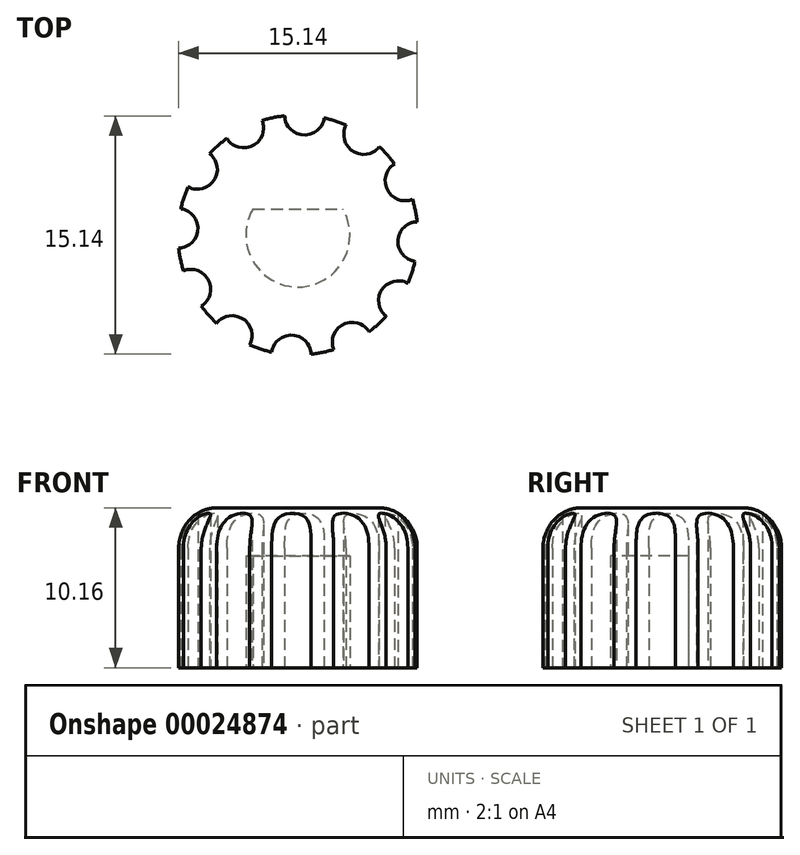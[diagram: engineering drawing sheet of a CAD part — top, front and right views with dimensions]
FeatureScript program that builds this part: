
annotation { "Feature Type Name" : "Feature", "Feature Type Description" : "" }
export const myFeature = defineFeature(function(context is Context, id is Id, definition is map)
    precondition{}
    {
        {
            var Q0;
            Q0=qCreatedBy(makeId("Top.planeOp"),FACE);
            var sketch = newSketch(context, id + "F0", { "sketchPlane" : qUnion([Q0])});
            skCircle(sketch, "E0", {"center": v(0, 0) * mm, "radius": 7.62 * mm});
            skSolve(sketch);
        }
        {
            var Q0;
            Q0=makeQuery(id+"F0.imprint","IMPRINT",FACE,{"disambiguationData":[TD([[makeQuery(id+"F0.imprint","IMPRINT",EDGE,{"derivedFrom":sQuery(id+"F0.wireOp",EDGE,"E0")}),1.0]])]});
            extrude(context, id + "F1", {"entities" : qUnion([Q0]), "oppositeDirection" : true, "depth" : 10.16 * mm});
        }
        {
            var Q0;
            Q0=makeQuery(id+"F1.opExtrude","CAP_FACE",FACE,{"disambiguationData":[OSD([sQuery(id+"F0.wireOp",EDGE,"E0")])],"isStart":false});
            var sketch = newSketch(context, id + "F2", { "sketchPlane" : qUnion([Q0])});
            skArc(sketch, "E1", {"start": v(2.86, -1.65) * mm, "mid": v(0, 3.3) * mm, "end": v(-2.86, -1.65) * mm});
            skLineSegment(sketch, "E2", {"start": v(-4.01, 3.3) * mm, "end": v(4.27, 3.3) * mm, "construction": true});
            skLineSegment(sketch, "E3", {"start": v(-2.86, -1.65) * mm, "end": v(2.86, -1.65) * mm});
            skSolve(sketch);
        }
        {
            var Q0;
            Q0=makeQuery(id+"F2.imprint","IMPRINT",FACE,{"disambiguationData":[TD([[makeQuery(id+"F2.imprint","IMPRINT",EDGE,{"derivedFrom":sQuery(id+"F2.wireOp",EDGE,"E1")}),1.0]])]});
            extrude(context, id + "F3", {"entities" : qUnion([Q0]), "operationType" : NewBodyOperationType.REMOVE, "oppositeDirection" : true, "depth" : 7.11 * mm});
        }
        {
            var Q0;
            Q0=makeQuery(id+"F1.opExtrude","CAP_EDGE",EDGE,{"disambiguationData":[OSD([sQuery(id+"F0.wireOp",EDGE,"E0")])],"isStart":true});
            fillet(context, id + "F4", {"entities" : qUnion([Q0]), "radius" : 2.54 * mm, "tangentPropagation" : true, "allowEdgeOverflow" : false});
        }
        {
            var Q0;
            Q0=makeQuery(id+"F1.opExtrude","CAP_FACE",FACE,{"disambiguationData":[OSD([sQuery(id+"F0.wireOp",EDGE,"E0")])],"isStart":false});
            var sketch = newSketch(context, id + "F5", { "sketchPlane" : qUnion([Q0])});
            skCircle(sketch, "E4", {"center": v(3.44, 6.8) * mm, "radius": 1.26 * mm});
            skCircle(sketch, "E5.1.0", {"center": v(-0.42, 7.6) * mm, "radius": 1.26 * mm});
            skCircle(sketch, "E5.2.0", {"center": v(-4.17, 6.38) * mm, "radius": 1.26 * mm});
            skCircle(sketch, "E5.3.0", {"center": v(-6.8, 3.44) * mm, "radius": 1.26 * mm});
            skCircle(sketch, "E5.4.0", {"center": v(-7.6, -0.42) * mm, "radius": 1.26 * mm});
            skCircle(sketch, "E5.5.0", {"center": v(-6.38, -4.17) * mm, "radius": 1.26 * mm});
            skCircle(sketch, "E5.6.0", {"center": v(-3.44, -6.8) * mm, "radius": 1.26 * mm});
            skCircle(sketch, "E5.7.0", {"center": v(0.42, -7.6) * mm, "radius": 1.26 * mm});
            skCircle(sketch, "E5.8.0", {"center": v(4.17, -6.38) * mm, "radius": 1.26 * mm});
            skCircle(sketch, "E5.9.0", {"center": v(6.8, -3.44) * mm, "radius": 1.26 * mm});
            skPoint(sketch, "E5.center", {"position": v(0, 0) * mm});
            skCircle(sketch, "E6.1.10.0", {"center": v(7.6, 0.42) * mm, "radius": 1.26 * mm});
            skCircle(sketch, "E7.1.11.0", {"center": v(6.38, 4.17) * mm, "radius": 1.26 * mm});
            skSolve(sketch);
        }
        {
            var Q0;
            {var subQ0=makeQuery(id+"F1.opExtrude","CAP_EDGE",EDGE,{"disambiguationData":[OSD([sQuery(id+"F0.wireOp",EDGE,"E0")])],"isStart":false});var subQ1=sQuery(id+"F5.wireOp",EDGE,"E5.2.0");var subQ3=makeQuery(id+"F5.imprint","INTERSECT",VERTEX,{"disambiguationData":[OD(0.0)],"derivedFrom":[subQ0,subQ1]});Q0=makeQuery(id+"F5.imprint","IMPRINT",FACE,{"disambiguationData":[TD([[makeQuery(id+"F5.imprint","IMPRINT",EDGE,{"disambiguationData":[TD([[subQ3,-1.0]])],"derivedFrom":subQ1}),1.0]])]});}
            var Q1;
            {var subQ0=makeQuery(id+"F1.opExtrude","CAP_EDGE",EDGE,{"disambiguationData":[OSD([sQuery(id+"F0.wireOp",EDGE,"E0")])],"isStart":false});var subQ1=sQuery(id+"F5.wireOp",EDGE,"E5.1.0");var subQ3=makeQuery(id+"F5.imprint","INTERSECT",VERTEX,{"disambiguationData":[OD(0.0)],"derivedFrom":[subQ0,subQ1]});Q1=makeQuery(id+"F5.imprint","IMPRINT",FACE,{"disambiguationData":[TD([[makeQuery(id+"F5.imprint","IMPRINT",EDGE,{"disambiguationData":[TD([[subQ3,-1.0]])],"derivedFrom":subQ1}),1.0]])]});}
            var Q2;
            {var subQ0=makeQuery(id+"F1.opExtrude","CAP_EDGE",EDGE,{"disambiguationData":[OSD([sQuery(id+"F0.wireOp",EDGE,"E0")])],"isStart":false});var subQ1=sQuery(id+"F5.wireOp",EDGE,"E4");var subQ3=makeQuery(id+"F5.imprint","INTERSECT",VERTEX,{"disambiguationData":[OD(0.0)],"derivedFrom":[subQ0,subQ1]});Q2=makeQuery(id+"F5.imprint","IMPRINT",FACE,{"disambiguationData":[TD([[makeQuery(id+"F5.imprint","IMPRINT",EDGE,{"disambiguationData":[TD([[subQ3,-1.0]])],"derivedFrom":subQ1}),1.0]])]});}
            var Q3;
            {var subQ0=makeQuery(id+"F1.opExtrude","CAP_EDGE",EDGE,{"disambiguationData":[OSD([sQuery(id+"F0.wireOp",EDGE,"E0")])],"isStart":false});var subQ1=sQuery(id+"F5.wireOp",EDGE,"E7.1.11.0");var subQ3=makeQuery(id+"F5.imprint","INTERSECT",VERTEX,{"disambiguationData":[OD(0.0)],"derivedFrom":[subQ0,subQ1]});Q3=makeQuery(id+"F5.imprint","IMPRINT",FACE,{"disambiguationData":[TD([[makeQuery(id+"F5.imprint","IMPRINT",EDGE,{"disambiguationData":[TD([[subQ3,-1.0]])],"derivedFrom":subQ1}),1.0]])]});}
            var Q4;
            {var subQ0=makeQuery(id+"F1.opExtrude","CAP_EDGE",EDGE,{"disambiguationData":[OSD([sQuery(id+"F0.wireOp",EDGE,"E0")])],"isStart":false});var subQ1=sQuery(id+"F5.wireOp",EDGE,"E6.1.10.0");var subQ3=makeQuery(id+"F5.imprint","INTERSECT",VERTEX,{"disambiguationData":[OD(0.0)],"derivedFrom":[subQ0,subQ1]});Q4=makeQuery(id+"F5.imprint","IMPRINT",FACE,{"disambiguationData":[TD([[makeQuery(id+"F5.imprint","IMPRINT",EDGE,{"disambiguationData":[TD([[subQ3,-1.0]])],"derivedFrom":subQ1}),1.0]])]});}
            var Q5;
            {var subQ0=makeQuery(id+"F1.opExtrude","CAP_EDGE",EDGE,{"disambiguationData":[OSD([sQuery(id+"F0.wireOp",EDGE,"E0")])],"isStart":false});var subQ1=sQuery(id+"F5.wireOp",EDGE,"E5.9.0");var subQ3=makeQuery(id+"F5.imprint","INTERSECT",VERTEX,{"disambiguationData":[OD(0.0)],"derivedFrom":[subQ0,subQ1]});Q5=makeQuery(id+"F5.imprint","IMPRINT",FACE,{"disambiguationData":[TD([[makeQuery(id+"F5.imprint","IMPRINT",EDGE,{"disambiguationData":[TD([[subQ3,1.0]])],"derivedFrom":subQ1}),1.0]])]});}
            var Q6;
            {var subQ0=makeQuery(id+"F1.opExtrude","CAP_EDGE",EDGE,{"disambiguationData":[OSD([sQuery(id+"F0.wireOp",EDGE,"E0")])],"isStart":false});var subQ1=sQuery(id+"F5.wireOp",EDGE,"E5.8.0");var subQ3=makeQuery(id+"F5.imprint","INTERSECT",VERTEX,{"disambiguationData":[OD(0.0)],"derivedFrom":[subQ0,subQ1]});Q6=makeQuery(id+"F5.imprint","IMPRINT",FACE,{"disambiguationData":[TD([[makeQuery(id+"F5.imprint","IMPRINT",EDGE,{"disambiguationData":[TD([[subQ3,1.0]])],"derivedFrom":subQ1}),1.0]])]});}
            var Q7;
            {var subQ0=makeQuery(id+"F1.opExtrude","CAP_EDGE",EDGE,{"disambiguationData":[OSD([sQuery(id+"F0.wireOp",EDGE,"E0")])],"isStart":false});var subQ1=sQuery(id+"F5.wireOp",EDGE,"E5.7.0");var subQ3=makeQuery(id+"F5.imprint","INTERSECT",VERTEX,{"disambiguationData":[OD(0.0)],"derivedFrom":[subQ0,subQ1]});Q7=makeQuery(id+"F5.imprint","IMPRINT",FACE,{"disambiguationData":[TD([[makeQuery(id+"F5.imprint","IMPRINT",EDGE,{"disambiguationData":[TD([[subQ3,1.0]])],"derivedFrom":subQ1}),1.0]])]});}
            var Q8;
            {var subQ0=makeQuery(id+"F1.opExtrude","CAP_EDGE",EDGE,{"disambiguationData":[OSD([sQuery(id+"F0.wireOp",EDGE,"E0")])],"isStart":false});var subQ1=sQuery(id+"F5.wireOp",EDGE,"E5.6.0");var subQ3=makeQuery(id+"F5.imprint","INTERSECT",VERTEX,{"disambiguationData":[OD(0.0)],"derivedFrom":[subQ0,subQ1]});Q8=makeQuery(id+"F5.imprint","IMPRINT",FACE,{"disambiguationData":[TD([[makeQuery(id+"F5.imprint","IMPRINT",EDGE,{"disambiguationData":[TD([[subQ3,1.0]])],"derivedFrom":subQ1}),1.0]])]});}
            var Q9;
            {var subQ0=makeQuery(id+"F1.opExtrude","CAP_EDGE",EDGE,{"disambiguationData":[OSD([sQuery(id+"F0.wireOp",EDGE,"E0")])],"isStart":false});var subQ1=sQuery(id+"F5.wireOp",EDGE,"E5.5.0");var subQ3=makeQuery(id+"F5.imprint","INTERSECT",VERTEX,{"disambiguationData":[OD(0.0)],"derivedFrom":[subQ0,subQ1]});Q9=makeQuery(id+"F5.imprint","IMPRINT",FACE,{"disambiguationData":[TD([[makeQuery(id+"F5.imprint","IMPRINT",EDGE,{"disambiguationData":[TD([[subQ3,1.0]])],"derivedFrom":subQ1}),1.0]])]});}
            var Q10;
            {var subQ0=makeQuery(id+"F1.opExtrude","CAP_EDGE",EDGE,{"disambiguationData":[OSD([sQuery(id+"F0.wireOp",EDGE,"E0")])],"isStart":false});var subQ1=sQuery(id+"F5.wireOp",EDGE,"E5.4.0");var subQ3=makeQuery(id+"F5.imprint","INTERSECT",VERTEX,{"disambiguationData":[OD(0.0)],"derivedFrom":[subQ0,subQ1]});Q10=makeQuery(id+"F5.imprint","IMPRINT",FACE,{"disambiguationData":[TD([[makeQuery(id+"F5.imprint","IMPRINT",EDGE,{"disambiguationData":[TD([[subQ3,1.0]])],"derivedFrom":subQ1}),1.0]])]});}
            var Q11;
            {var subQ0=makeQuery(id+"F1.opExtrude","CAP_EDGE",EDGE,{"disambiguationData":[OSD([sQuery(id+"F0.wireOp",EDGE,"E0")])],"isStart":false});var subQ1=sQuery(id+"F5.wireOp",EDGE,"E5.3.0");var subQ3=makeQuery(id+"F5.imprint","INTERSECT",VERTEX,{"disambiguationData":[OD(0.0)],"derivedFrom":[subQ0,subQ1]});Q11=makeQuery(id+"F5.imprint","IMPRINT",FACE,{"disambiguationData":[TD([[makeQuery(id+"F5.imprint","IMPRINT",EDGE,{"disambiguationData":[TD([[subQ3,-1.0]])],"derivedFrom":subQ1}),1.0]])]});}
            extrude(context, id + "F6", {"entities" : qUnion([Q0, Q1, Q2, Q3, Q4, Q5, Q6, Q7, Q8, Q9, Q10, Q11]), "operationType" : NewBodyOperationType.REMOVE, "oppositeDirection" : true, "depth" : 25.4 * mm});
        }
    });
